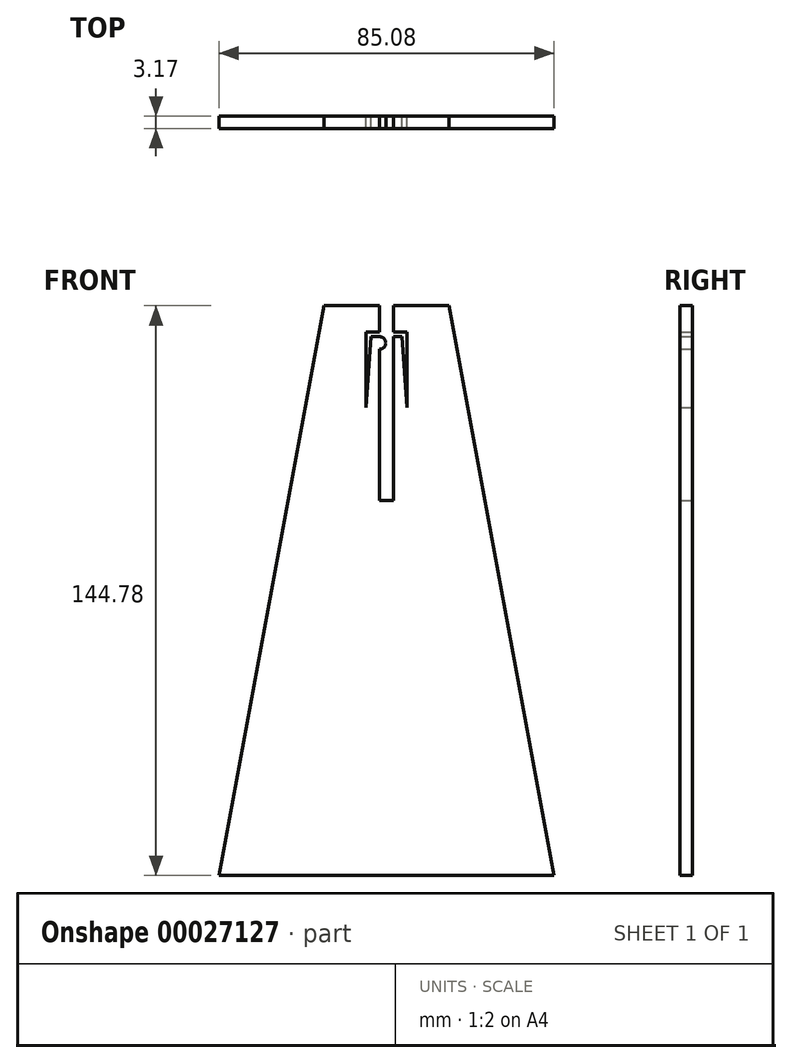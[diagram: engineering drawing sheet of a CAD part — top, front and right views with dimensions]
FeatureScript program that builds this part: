
annotation { "Feature Type Name" : "Feature", "Feature Type Description" : "" }
export const myFeature = defineFeature(function(context is Context, id is Id, definition is map)
    precondition{}
    {
        {
            var Q0;
            Q0=qCreatedBy(makeId("Front.planeOp"),FACE);
            var sketch = newSketch(context, id + "F0", { "sketchPlane" : qUnion([Q0])});
            skLineSegment(sketch, "E0.bottom", {"start": v(-31.8, 90.9) * mm, "end": v(-17.67, 90.9) * mm});
            skLineSegment(sketch, "E0.top", {"start": v(-58.44, -53.88) * mm, "end": v(-15.9, -53.88) * mm});
            skLineSegment(sketch, "E0.right", {"start": v(-15.9, 41.37) * mm, "end": v(-15.9, -53.88) * mm});
            skLineSegment(sketch, "E1.top", {"start": v(-17.67, 41.37) * mm, "end": v(-15.9, 41.37) * mm});
            skLineSegment(sketch, "E1.left", {"start": v(-17.67, 90.9) * mm, "end": v(-17.67, 84.24) * mm});
            skLineSegment(sketch, "E2", {"start": v(-17.67, 84.24) * mm, "end": v(-21.06, 84.24) * mm});
            skLineSegment(sketch, "E3", {"start": v(-21.06, 84.24) * mm, "end": v(-21.06, 65.04) * mm});
            skLineSegment(sketch, "E4", {"start": v(-21.06, 65.04) * mm, "end": v(-19.82, 83) * mm});
            skLineSegment(sketch, "E5", {"start": v(-19.82, 83) * mm, "end": v(-17.67, 83) * mm});
            skArc(sketch, "E6", {"start": v(-17.67, 79.83) * mm, "mid": v(-16.09, 81.41) * mm, "end": v(-17.67, 83) * mm});
            skLineSegment(sketch, "E7.trimOffspring", {"start": v(-17.67, 83) * mm, "end": v(-17.67, 41.37) * mm});
            skLineSegment(sketch, "E8.MirrorCS", {"start": v(-11.97, 83) * mm, "end": v(-14.12, 83) * mm});
            skLineSegment(sketch, "E9.MirrorCS", {"start": v(-14.12, 84.24) * mm, "end": v(-10.74, 84.24) * mm});
            skLineSegment(sketch, "E10.MirrorCS", {"start": v(-14.12, 41.37) * mm, "end": v(-15.9, 41.37) * mm});
            skLineSegment(sketch, "E11.MirrorCS", {"start": v(26.64, -53.88) * mm, "end": v(-15.9, -53.88) * mm});
            skLineSegment(sketch, "E12.MirrorCS", {"start": v(0, 90.9) * mm, "end": v(-14.12, 90.9) * mm});
            skArc(sketch, "E13.MirrorCS", {"start": v(-14.12, 79.83) * mm, "mid": v(-15.7, 81.41) * mm, "end": v(-14.12, 83) * mm});
            skLineSegment(sketch, "E14.MirrorCS", {"start": v(-14.12, 90.9) * mm, "end": v(-14.12, 84.24) * mm});
            skLineSegment(sketch, "E15.MirrorCS", {"start": v(-10.74, 84.24) * mm, "end": v(-10.74, 65.04) * mm});
            skLineSegment(sketch, "E16.MirrorCS", {"start": v(-14.12, 83) * mm, "end": v(-14.12, 41.37) * mm});
            skLineSegment(sketch, "E17.MirrorCS", {"start": v(-10.74, 65.04) * mm, "end": v(-11.97, 83) * mm});
            skLineSegment(sketch, "E18", {"start": v(0, 90.9) * mm, "end": v(26.64, -53.88) * mm});
            skPoint(sketch, "E19.MirrorCS.start.orphan", {"position": v(36.68, 90.9) * mm});
            skPoint(sketch, "E20.orphan", {"position": v(36.68, -53.88) * mm});
            skLineSegment(sketch, "E21.MirrorCS", {"start": v(-31.8, 90.9) * mm, "end": v(-58.44, -53.88) * mm});
            skPoint(sketch, "E0.left.start.orphan", {"position": v(-68.47, 90.9) * mm});
            skPoint(sketch, "E22.orphan", {"position": v(-68.47, -53.88) * mm});
            skSolve(sketch);
        }
        {
            var Q0;
            Q0=makeQuery(id+"F0.imprint","IMPRINT",FACE,{"disambiguationData":[TD([[makeQuery(id+"F0.imprint","IMPRINT",EDGE,{"derivedFrom":sQuery(id+"F0.wireOp",EDGE,"E0.bottom")}),-1.0]])]});
            var Q1;
            Q1=makeQuery(id+"F0.imprint","IMPRINT",FACE,{"disambiguationData":[TD([[makeQuery(id+"F0.imprint","IMPRINT",EDGE,{"derivedFrom":sQuery(id+"F0.wireOp",EDGE,"E0.right")}),1.0]])]});
            var Q2;
            {var subQ1=sQuery(id+"F0.wireOp",EDGE,"E6");Q2=makeQuery(id+"F0.imprint","IMPRINT",FACE,{"disambiguationData":[TD([[makeQuery(id+"F0.imprint","IMPRINT",EDGE,{"derivedFrom":subQ1}),1.0]])]});}
            var Q3;
            {var subQ1=sQuery(id+"F0.wireOp",EDGE,"E13.MirrorCS");Q3=makeQuery(id+"F0.imprint","IMPRINT",FACE,{"disambiguationData":[TD([[makeQuery(id+"F0.imprint","IMPRINT",EDGE,{"derivedFrom":subQ1}),-1.0]])]});}
            var Q4;
            Q4=makeQuery(id+"F0.imprint","IMPRINT",FACE,{"disambiguationData":[TD([[makeQuery(id+"F0.imprint","IMPRINT",EDGE,{"derivedFrom":sQuery(id+"F0.wireOp",EDGE,"E0.right")}),-1.0]])]});
            extrude(context, id + "F1", {"entities" : qUnion([Q0, Q1, Q2, Q3, Q4]), "depth" : 3.17 * mm});
        }
    });
